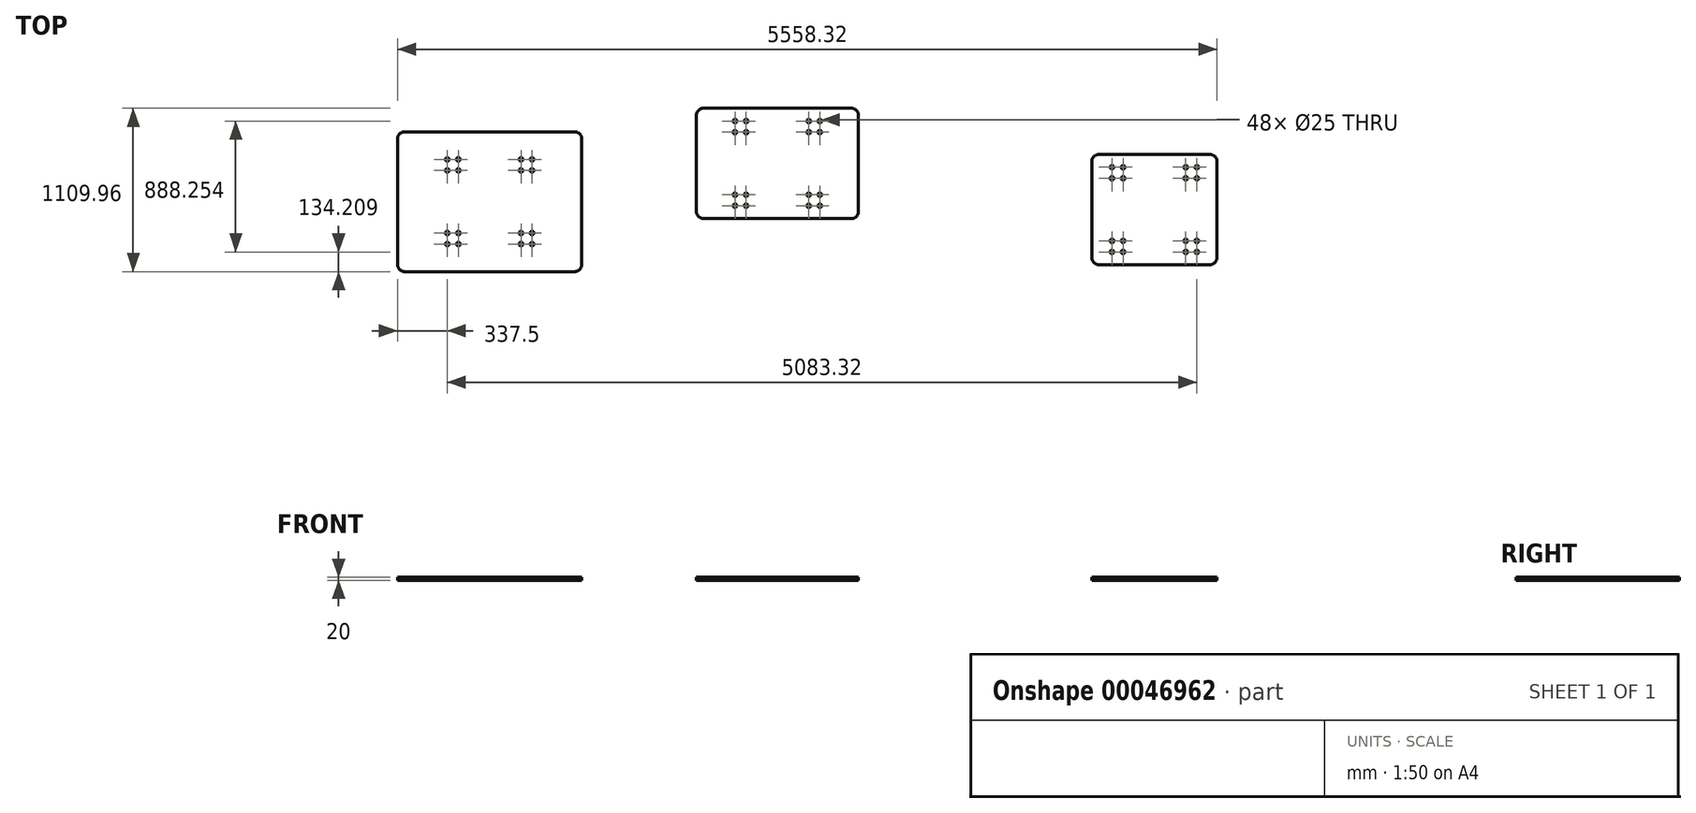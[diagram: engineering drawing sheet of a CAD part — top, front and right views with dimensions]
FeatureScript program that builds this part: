
annotation { "Feature Type Name" : "Feature", "Feature Type Description" : "" }
export const myFeature = defineFeature(function(context is Context, id is Id, definition is map)
    precondition{}
    {
        {
            var Q0;
            Q0=qCreatedBy(makeId("Top.planeOp"),FACE);
            var sketch = newSketch(context, id + "F0", { "sketchPlane" : qUnion([Q0])});
            skLineSegment(sketch, "E0", {"start": v(0, 0) * mm, "end": v(-758.12, 0) * mm, "construction": true});
            skLineSegment(sketch, "E1", {"start": v(0, 0) * mm, "end": v(0, 528.37) * mm, "construction": true});
            skLineSegment(sketch, "E2.rect.bottom", {"start": v(-250, 250) * mm, "end": v(250, 250) * mm, "construction": true});
            skLineSegment(sketch, "E2.rect.top", {"start": v(-250, -250) * mm, "end": v(250, -250) * mm, "construction": true});
            skLineSegment(sketch, "E2.rect.left", {"start": v(-250, 250) * mm, "end": v(-250, -250) * mm, "construction": true});
            skLineSegment(sketch, "E2.rect.right", {"start": v(250, 250) * mm, "end": v(250, -250) * mm, "construction": true});
            skPoint(sketch, "E2.rect.middle", {"position": v(0, 0) * mm});
            skLineSegment(sketch, "E3.rect.bottom", {"start": v(-287.5, 212.5) * mm, "end": v(-212.5, 212.5) * mm, "construction": true});
            skLineSegment(sketch, "E3.rect.top", {"start": v(-287.5, 287.5) * mm, "end": v(-212.5, 287.5) * mm, "construction": true});
            skLineSegment(sketch, "E3.rect.left", {"start": v(-287.5, 212.5) * mm, "end": v(-287.5, 287.5) * mm, "construction": true});
            skLineSegment(sketch, "E3.rect.right", {"start": v(-212.5, 212.5) * mm, "end": v(-212.5, 287.5) * mm, "construction": true});
            skPoint(sketch, "E3.rect.middle", {"position": v(-250, 250) * mm});
            skCircle(sketch, "E4", {"center": v(-287.5, 287.5) * mm, "radius": 12.5 * mm});
            skCircle(sketch, "E5", {"center": v(-212.5, 287.5) * mm, "radius": 12.5 * mm});
            skCircle(sketch, "E6", {"center": v(-287.5, 212.5) * mm, "radius": 12.5 * mm});
            skCircle(sketch, "E7", {"center": v(-212.5, 212.5) * mm, "radius": 12.5 * mm});
            skLineSegment(sketch, "E8.MirrorCS", {"start": v(287.5, 287.5) * mm, "end": v(212.5, 287.5) * mm, "construction": true});
            skCircle(sketch, "E9.MirrorC", {"center": v(212.5, 287.5) * mm, "radius": 12.5 * mm});
            skCircle(sketch, "E10.MirrorC", {"center": v(287.5, 287.5) * mm, "radius": 12.5 * mm});
            skPoint(sketch, "E11.MirrorP", {"position": v(250, 250) * mm});
            skLineSegment(sketch, "E12.MirrorCS", {"start": v(287.5, 212.5) * mm, "end": v(287.5, 287.5) * mm, "construction": true});
            skLineSegment(sketch, "E13.MirrorCS", {"start": v(212.5, 212.5) * mm, "end": v(212.5, 287.5) * mm, "construction": true});
            skLineSegment(sketch, "E14.MirrorCS", {"start": v(287.5, 212.5) * mm, "end": v(212.5, 212.5) * mm, "construction": true});
            skCircle(sketch, "E15.MirrorC", {"center": v(212.5, 212.5) * mm, "radius": 12.5 * mm});
            skCircle(sketch, "E16.MirrorC", {"center": v(287.5, 212.5) * mm, "radius": 12.5 * mm});
            skCircle(sketch, "E17.MirrorC", {"center": v(287.5, -287.5) * mm, "radius": 12.5 * mm});
            skCircle(sketch, "E18.MirrorC", {"center": v(212.5, -287.5) * mm, "radius": 12.5 * mm});
            skCircle(sketch, "E19.MirrorC", {"center": v(-212.5, -287.5) * mm, "radius": 12.5 * mm});
            skCircle(sketch, "E20.MirrorC", {"center": v(-287.5, -287.5) * mm, "radius": 12.5 * mm});
            skCircle(sketch, "E21.MirrorC", {"center": v(287.5, -212.5) * mm, "radius": 12.5 * mm});
            skCircle(sketch, "E22.MirrorC", {"center": v(212.5, -212.5) * mm, "radius": 12.5 * mm});
            skCircle(sketch, "E23.MirrorC", {"center": v(-212.5, -212.5) * mm, "radius": 12.5 * mm});
            skCircle(sketch, "E24.MirrorC", {"center": v(-287.5, -212.5) * mm, "radius": 12.5 * mm});
            skLineSegment(sketch, "E25.MirrorCS", {"start": v(287.5, -287.5) * mm, "end": v(212.5, -287.5) * mm, "construction": true});
            skLineSegment(sketch, "E26.MirrorCS", {"start": v(-287.5, -287.5) * mm, "end": v(-212.5, -287.5) * mm, "construction": true});
            skLineSegment(sketch, "E27.MirrorCS", {"start": v(-250, -250) * mm, "end": v(250, -250) * mm});
            skLineSegment(sketch, "E28.MirrorCS", {"start": v(287.5, -212.5) * mm, "end": v(287.5, -287.5) * mm, "construction": true});
            skLineSegment(sketch, "E29.MirrorCS", {"start": v(212.5, -212.5) * mm, "end": v(212.5, -287.5) * mm, "construction": true});
            skLineSegment(sketch, "E30.MirrorCS", {"start": v(-212.5, -212.5) * mm, "end": v(-212.5, -287.5) * mm, "construction": true});
            skLineSegment(sketch, "E31.MirrorCS", {"start": v(-287.5, -212.5) * mm, "end": v(-287.5, -287.5) * mm, "construction": true});
            skPoint(sketch, "E32.MirrorP", {"position": v(250, -250) * mm});
            skPoint(sketch, "E33.MirrorP", {"position": v(-250, -250) * mm});
            skLineSegment(sketch, "E34.MirrorCS", {"start": v(287.5, -212.5) * mm, "end": v(212.5, -212.5) * mm, "construction": true});
            skLineSegment(sketch, "E35.MirrorCS", {"start": v(-287.5, -212.5) * mm, "end": v(-212.5, -212.5) * mm, "construction": true});
            skLineSegment(sketch, "E36.rect.bottom", {"start": v(-625, 475) * mm, "end": v(625, 475) * mm});
            skLineSegment(sketch, "E36.rect.top", {"start": v(-625, -475) * mm, "end": v(625, -475) * mm});
            skLineSegment(sketch, "E36.rect.left", {"start": v(-625, 475) * mm, "end": v(-625, -475) * mm});
            skLineSegment(sketch, "E36.rect.right", {"start": v(625, 475) * mm, "end": v(625, -475) * mm});
            skSolve(sketch);
        }
        {
            var Q0;
            Q0=qSketchRegion(id+"F0",true);
            extrude(context, id + "F1", {"entities" : qUnion([Q0]), "depth" : 20 * mm});
        }
        {
            var Q0;
            Q0=makeQuery(id+"F1.opExtrude","SWEPT_EDGE",EDGE,{"disambiguationData":[OSD([sQuery(id+"F0.wireOp",EDGE,"E36.rect.bottom"),sQuery(id+"F0.wireOp",EDGE,"E36.rect.left")])]});
            var Q1;
            Q1=makeQuery(id+"F1.opExtrude","SWEPT_EDGE",EDGE,{"disambiguationData":[OSD([sQuery(id+"F0.wireOp",EDGE,"E36.rect.bottom"),sQuery(id+"F0.wireOp",EDGE,"E36.rect.right")])]});
            var Q2;
            Q2=makeQuery(id+"F1.opExtrude","SWEPT_EDGE",EDGE,{"disambiguationData":[OSD([sQuery(id+"F0.wireOp",EDGE,"E36.rect.top"),sQuery(id+"F0.wireOp",EDGE,"E36.rect.left")])]});
            var Q3;
            Q3=makeQuery(id+"F1.opExtrude","SWEPT_EDGE",EDGE,{"disambiguationData":[OSD([sQuery(id+"F0.wireOp",EDGE,"E36.rect.top"),sQuery(id+"F0.wireOp",EDGE,"E36.rect.right")])]});
            fillet(context, id + "F2", {"entities" : qUnion([Q0, Q1, Q2, Q3]), "radius" : 50 * mm, "tangentPropagation" : true, "allowEdgeOverflow" : false});
        }
        {
            var Q0;
            Q0=qCreatedBy(makeId("Top.planeOp"),FACE);
            var sketch = newSketch(context, id + "F3", { "sketchPlane" : qUnion([Q0])});
            skLineSegment(sketch, "E37", {"start": v(1951.56, 259.96) * mm, "end": v(1393.44, 259.96) * mm, "construction": true});
            skLineSegment(sketch, "E38", {"start": v(1951.56, 259.96) * mm, "end": v(1951.56, 638.33) * mm, "construction": true});
            skLineSegment(sketch, "E39.rect.bottom", {"start": v(1701.56, 509.96) * mm, "end": v(2201.56, 509.96) * mm, "construction": true});
            skLineSegment(sketch, "E39.rect.top", {"start": v(1701.56, 9.96) * mm, "end": v(2201.56, 9.96) * mm, "construction": true});
            skLineSegment(sketch, "E39.rect.left", {"start": v(1701.56, 509.96) * mm, "end": v(1701.56, 9.96) * mm, "construction": true});
            skLineSegment(sketch, "E39.rect.right", {"start": v(2201.56, 509.96) * mm, "end": v(2201.56, 9.96) * mm, "construction": true});
            skPoint(sketch, "E39.rect.middle", {"position": v(1951.56, 259.96) * mm});
            skLineSegment(sketch, "E40.rect.bottom", {"start": v(1664.06, 472.46) * mm, "end": v(1739.06, 472.46) * mm, "construction": true});
            skLineSegment(sketch, "E40.rect.top", {"start": v(1664.06, 547.46) * mm, "end": v(1739.06, 547.46) * mm, "construction": true});
            skLineSegment(sketch, "E40.rect.left", {"start": v(1664.06, 472.46) * mm, "end": v(1664.06, 547.46) * mm, "construction": true});
            skLineSegment(sketch, "E40.rect.right", {"start": v(1739.06, 472.46) * mm, "end": v(1739.06, 547.46) * mm, "construction": true});
            skPoint(sketch, "E40.rect.middle", {"position": v(1701.56, 509.96) * mm});
            skCircle(sketch, "E41", {"center": v(1664.06, 547.46) * mm, "radius": 12.5 * mm});
            skCircle(sketch, "E42", {"center": v(1739.06, 547.46) * mm, "radius": 12.5 * mm});
            skCircle(sketch, "E43", {"center": v(1664.06, 472.46) * mm, "radius": 12.5 * mm});
            skCircle(sketch, "E44", {"center": v(1739.06, 472.46) * mm, "radius": 12.5 * mm});
            skLineSegment(sketch, "E45.MirrorCS", {"start": v(2239.06, 547.46) * mm, "end": v(2164.06, 547.46) * mm, "construction": true});
            skCircle(sketch, "E46.MirrorC", {"center": v(2164.06, 547.46) * mm, "radius": 12.5 * mm});
            skCircle(sketch, "E47.MirrorC", {"center": v(2239.06, 547.46) * mm, "radius": 12.5 * mm});
            skPoint(sketch, "E48.MirrorP", {"position": v(2201.56, 509.96) * mm});
            skLineSegment(sketch, "E49.MirrorCS", {"start": v(2239.06, 472.46) * mm, "end": v(2239.06, 547.46) * mm, "construction": true});
            skLineSegment(sketch, "E50.MirrorCS", {"start": v(2164.06, 472.46) * mm, "end": v(2164.06, 547.46) * mm, "construction": true});
            skLineSegment(sketch, "E51.MirrorCS", {"start": v(2239.06, 472.46) * mm, "end": v(2164.06, 472.46) * mm, "construction": true});
            skCircle(sketch, "E52.MirrorC", {"center": v(2164.06, 472.46) * mm, "radius": 12.5 * mm});
            skCircle(sketch, "E53.MirrorC", {"center": v(2239.06, 472.46) * mm, "radius": 12.5 * mm});
            skCircle(sketch, "E54.MirrorC", {"center": v(2239.06, -27.54) * mm, "radius": 12.5 * mm});
            skCircle(sketch, "E55.MirrorC", {"center": v(2164.06, -27.54) * mm, "radius": 12.5 * mm});
            skCircle(sketch, "E56.MirrorC", {"center": v(1739.06, -27.54) * mm, "radius": 12.5 * mm});
            skCircle(sketch, "E57.MirrorC", {"center": v(1664.06, -27.54) * mm, "radius": 12.5 * mm});
            skCircle(sketch, "E58.MirrorC", {"center": v(2239.06, 47.46) * mm, "radius": 12.5 * mm});
            skCircle(sketch, "E59.MirrorC", {"center": v(2164.06, 47.46) * mm, "radius": 12.5 * mm});
            skCircle(sketch, "E60.MirrorC", {"center": v(1739.06, 47.46) * mm, "radius": 12.5 * mm});
            skCircle(sketch, "E61.MirrorC", {"center": v(1664.06, 47.46) * mm, "radius": 12.5 * mm});
            skLineSegment(sketch, "E62.MirrorCS", {"start": v(2239.06, -27.54) * mm, "end": v(2164.06, -27.54) * mm, "construction": true});
            skLineSegment(sketch, "E63.MirrorCS", {"start": v(1664.06, -27.54) * mm, "end": v(1739.06, -27.54) * mm, "construction": true});
            skLineSegment(sketch, "E64.MirrorCS", {"start": v(1701.56, 9.96) * mm, "end": v(2201.56, 9.96) * mm});
            skLineSegment(sketch, "E65.MirrorCS", {"start": v(2239.06, 47.46) * mm, "end": v(2239.06, -27.54) * mm, "construction": true});
            skLineSegment(sketch, "E66.MirrorCS", {"start": v(2164.06, 47.46) * mm, "end": v(2164.06, -27.54) * mm, "construction": true});
            skLineSegment(sketch, "E67.MirrorCS", {"start": v(1739.06, 47.46) * mm, "end": v(1739.06, -27.54) * mm, "construction": true});
            skLineSegment(sketch, "E68.MirrorCS", {"start": v(1664.06, 47.46) * mm, "end": v(1664.06, -27.54) * mm, "construction": true});
            skPoint(sketch, "E69.MirrorP", {"position": v(2201.56, 9.96) * mm});
            skPoint(sketch, "E70.MirrorP", {"position": v(1701.56, 9.96) * mm});
            skLineSegment(sketch, "E71.MirrorCS", {"start": v(2239.06, 47.46) * mm, "end": v(2164.06, 47.46) * mm, "construction": true});
            skLineSegment(sketch, "E72.MirrorCS", {"start": v(1664.06, 47.46) * mm, "end": v(1739.06, 47.46) * mm, "construction": true});
            skLineSegment(sketch, "E73.rect.bottom", {"start": v(1401.56, 634.96) * mm, "end": v(2501.56, 634.96) * mm});
            skLineSegment(sketch, "E73.rect.top", {"start": v(1401.56, -115.04) * mm, "end": v(2501.56, -115.04) * mm});
            skLineSegment(sketch, "E73.rect.left", {"start": v(1401.56, 634.96) * mm, "end": v(1401.56, -115.04) * mm});
            skLineSegment(sketch, "E73.rect.right", {"start": v(2501.56, 634.96) * mm, "end": v(2501.56, -115.04) * mm});
            skSolve(sketch);
        }
        {
            var Q0;
            Q0=qSketchRegion(id+"F3",true);
            extrude(context, id + "F4", {"entities" : qUnion([Q0]), "depth" : 20 * mm});
        }
        {
            var Q0;
            Q0=makeQuery(id+"F4.opExtrude","SWEPT_EDGE",EDGE,{"disambiguationData":[OSD([sQuery(id+"F3.wireOp",EDGE,"E73.rect.bottom"),sQuery(id+"F3.wireOp",EDGE,"E73.rect.left")])]});
            var Q1;
            Q1=makeQuery(id+"F4.opExtrude","SWEPT_EDGE",EDGE,{"disambiguationData":[OSD([sQuery(id+"F3.wireOp",EDGE,"E73.rect.top"),sQuery(id+"F3.wireOp",EDGE,"E73.rect.left")])]});
            var Q2;
            Q2=makeQuery(id+"F4.opExtrude","SWEPT_EDGE",EDGE,{"disambiguationData":[OSD([sQuery(id+"F3.wireOp",EDGE,"E73.rect.bottom"),sQuery(id+"F3.wireOp",EDGE,"E73.rect.right")])]});
            var Q3;
            Q3=makeQuery(id+"F4.opExtrude","SWEPT_EDGE",EDGE,{"disambiguationData":[OSD([sQuery(id+"F3.wireOp",EDGE,"E73.rect.top"),sQuery(id+"F3.wireOp",EDGE,"E73.rect.right")])]});
            fillet(context, id + "F5", {"entities" : qUnion([Q0, Q1, Q2, Q3]), "radius" : 50 * mm, "tangentPropagation" : true, "allowEdgeOverflow" : false});
        }
        {
            var Q0;
            Q0=qCreatedBy(makeId("Top.planeOp"),FACE);
            var sketch = newSketch(context, id + "F6", { "sketchPlane" : qUnion([Q0])});
            skLineSegment(sketch, "E74", {"start": v(4508.32, -53.3) * mm, "end": v(3950.2, -53.3) * mm, "construction": true});
            skLineSegment(sketch, "E75", {"start": v(4508.32, -53.3) * mm, "end": v(4508.32, 325.08) * mm, "construction": true});
            skLineSegment(sketch, "E76.rect.bottom", {"start": v(4258.32, 196.7) * mm, "end": v(4758.32, 196.7) * mm, "construction": true});
            skLineSegment(sketch, "E76.rect.top", {"start": v(4258.32, -303.3) * mm, "end": v(4758.32, -303.3) * mm, "construction": true});
            skLineSegment(sketch, "E76.rect.left", {"start": v(4258.32, 196.7) * mm, "end": v(4258.32, -303.3) * mm, "construction": true});
            skLineSegment(sketch, "E76.rect.right", {"start": v(4758.32, 196.7) * mm, "end": v(4758.32, -303.3) * mm, "construction": true});
            skPoint(sketch, "E76.rect.middle", {"position": v(4508.32, -53.3) * mm});
            skLineSegment(sketch, "E77.rect.bottom", {"start": v(4220.82, 159.2) * mm, "end": v(4295.82, 159.2) * mm, "construction": true});
            skLineSegment(sketch, "E77.rect.top", {"start": v(4220.82, 234.2) * mm, "end": v(4295.82, 234.2) * mm, "construction": true});
            skLineSegment(sketch, "E77.rect.left", {"start": v(4220.82, 159.2) * mm, "end": v(4220.82, 234.2) * mm, "construction": true});
            skLineSegment(sketch, "E77.rect.right", {"start": v(4295.82, 159.2) * mm, "end": v(4295.82, 234.2) * mm, "construction": true});
            skPoint(sketch, "E77.rect.middle", {"position": v(4258.32, 196.7) * mm});
            skCircle(sketch, "E78", {"center": v(4220.82, 234.2) * mm, "radius": 12.5 * mm});
            skCircle(sketch, "E79", {"center": v(4295.82, 234.2) * mm, "radius": 12.5 * mm});
            skCircle(sketch, "E80", {"center": v(4220.82, 159.2) * mm, "radius": 12.5 * mm});
            skCircle(sketch, "E81", {"center": v(4295.82, 159.2) * mm, "radius": 12.5 * mm});
            skLineSegment(sketch, "E82.MirrorCS", {"start": v(4795.82, 234.2) * mm, "end": v(4720.82, 234.2) * mm, "construction": true});
            skCircle(sketch, "E83.MirrorC", {"center": v(4720.82, 234.2) * mm, "radius": 12.5 * mm});
            skCircle(sketch, "E84.MirrorC", {"center": v(4795.82, 234.2) * mm, "radius": 12.5 * mm});
            skPoint(sketch, "E85.MirrorP", {"position": v(4758.32, 196.7) * mm});
            skLineSegment(sketch, "E86.MirrorCS", {"start": v(4795.82, 159.2) * mm, "end": v(4795.82, 234.2) * mm, "construction": true});
            skLineSegment(sketch, "E87.MirrorCS", {"start": v(4720.82, 159.2) * mm, "end": v(4720.82, 234.2) * mm, "construction": true});
            skLineSegment(sketch, "E88.MirrorCS", {"start": v(4795.82, 159.2) * mm, "end": v(4720.82, 159.2) * mm, "construction": true});
            skCircle(sketch, "E89.MirrorC", {"center": v(4720.82, 159.2) * mm, "radius": 12.5 * mm});
            skCircle(sketch, "E90.MirrorC", {"center": v(4795.82, 159.2) * mm, "radius": 12.5 * mm});
            skCircle(sketch, "E91.MirrorC", {"center": v(4795.82, -340.8) * mm, "radius": 12.5 * mm});
            skCircle(sketch, "E92.MirrorC", {"center": v(4720.82, -340.8) * mm, "radius": 12.5 * mm});
            skCircle(sketch, "E93.MirrorC", {"center": v(4295.82, -340.8) * mm, "radius": 12.5 * mm});
            skCircle(sketch, "E94.MirrorC", {"center": v(4220.82, -340.8) * mm, "radius": 12.5 * mm});
            skCircle(sketch, "E95.MirrorC", {"center": v(4795.82, -265.8) * mm, "radius": 12.5 * mm});
            skCircle(sketch, "E96.MirrorC", {"center": v(4720.82, -265.8) * mm, "radius": 12.5 * mm});
            skCircle(sketch, "E97.MirrorC", {"center": v(4295.82, -265.8) * mm, "radius": 12.5 * mm});
            skCircle(sketch, "E98.MirrorC", {"center": v(4220.82, -265.8) * mm, "radius": 12.5 * mm});
            skLineSegment(sketch, "E99.MirrorCS", {"start": v(4795.82, -340.8) * mm, "end": v(4720.82, -340.8) * mm, "construction": true});
            skLineSegment(sketch, "E100.MirrorCS", {"start": v(4220.82, -340.8) * mm, "end": v(4295.82, -340.8) * mm, "construction": true});
            skLineSegment(sketch, "E101.MirrorCS", {"start": v(4258.32, -303.3) * mm, "end": v(4758.32, -303.3) * mm});
            skLineSegment(sketch, "E102.MirrorCS", {"start": v(4795.82, -265.8) * mm, "end": v(4795.82, -340.8) * mm, "construction": true});
            skLineSegment(sketch, "E103.MirrorCS", {"start": v(4720.82, -265.8) * mm, "end": v(4720.82, -340.8) * mm, "construction": true});
            skLineSegment(sketch, "E104.MirrorCS", {"start": v(4295.82, -265.8) * mm, "end": v(4295.82, -340.8) * mm, "construction": true});
            skLineSegment(sketch, "E105.MirrorCS", {"start": v(4220.82, -265.8) * mm, "end": v(4220.82, -340.8) * mm, "construction": true});
            skPoint(sketch, "E106.MirrorP", {"position": v(4758.32, -303.3) * mm});
            skPoint(sketch, "E107.MirrorP", {"position": v(4258.32, -303.3) * mm});
            skLineSegment(sketch, "E108.MirrorCS", {"start": v(4795.82, -265.8) * mm, "end": v(4720.82, -265.8) * mm, "construction": true});
            skLineSegment(sketch, "E109.MirrorCS", {"start": v(4220.82, -265.8) * mm, "end": v(4295.82, -265.8) * mm, "construction": true});
            skLineSegment(sketch, "E110.rect.bottom", {"start": v(4083.32, 321.7) * mm, "end": v(4933.32, 321.7) * mm});
            skLineSegment(sketch, "E110.rect.top", {"start": v(4083.32, -428.3) * mm, "end": v(4933.32, -428.3) * mm});
            skLineSegment(sketch, "E110.rect.left", {"start": v(4083.32, 321.7) * mm, "end": v(4083.32, -428.3) * mm});
            skLineSegment(sketch, "E110.rect.right", {"start": v(4933.32, 321.7) * mm, "end": v(4933.32, -428.3) * mm});
            skSolve(sketch);
        }
        {
            var Q0;
            Q0=qSketchRegion(id+"F6",true);
            extrude(context, id + "F7", {"entities" : qUnion([Q0]), "depth" : 20 * mm});
        }
        {
            var Q0;
            Q0=makeQuery(id+"F7.opExtrude","SWEPT_EDGE",EDGE,{"disambiguationData":[OSD([sQuery(id+"F6.wireOp",EDGE,"E110.rect.bottom"),sQuery(id+"F6.wireOp",EDGE,"E110.rect.left")])]});
            var Q1;
            Q1=makeQuery(id+"F7.opExtrude","SWEPT_EDGE",EDGE,{"disambiguationData":[OSD([sQuery(id+"F6.wireOp",EDGE,"E110.rect.bottom"),sQuery(id+"F6.wireOp",EDGE,"E110.rect.right")])]});
            var Q2;
            Q2=makeQuery(id+"F7.opExtrude","SWEPT_EDGE",EDGE,{"disambiguationData":[OSD([sQuery(id+"F6.wireOp",EDGE,"E110.rect.top"),sQuery(id+"F6.wireOp",EDGE,"E110.rect.right")])]});
            var Q3;
            Q3=makeQuery(id+"F7.opExtrude","SWEPT_EDGE",EDGE,{"disambiguationData":[OSD([sQuery(id+"F6.wireOp",EDGE,"E110.rect.top"),sQuery(id+"F6.wireOp",EDGE,"E110.rect.left")])]});
            fillet(context, id + "F8", {"entities" : qUnion([Q0, Q1, Q2, Q3]), "radius" : 50 * mm, "tangentPropagation" : true, "allowEdgeOverflow" : false});
        }
    });
